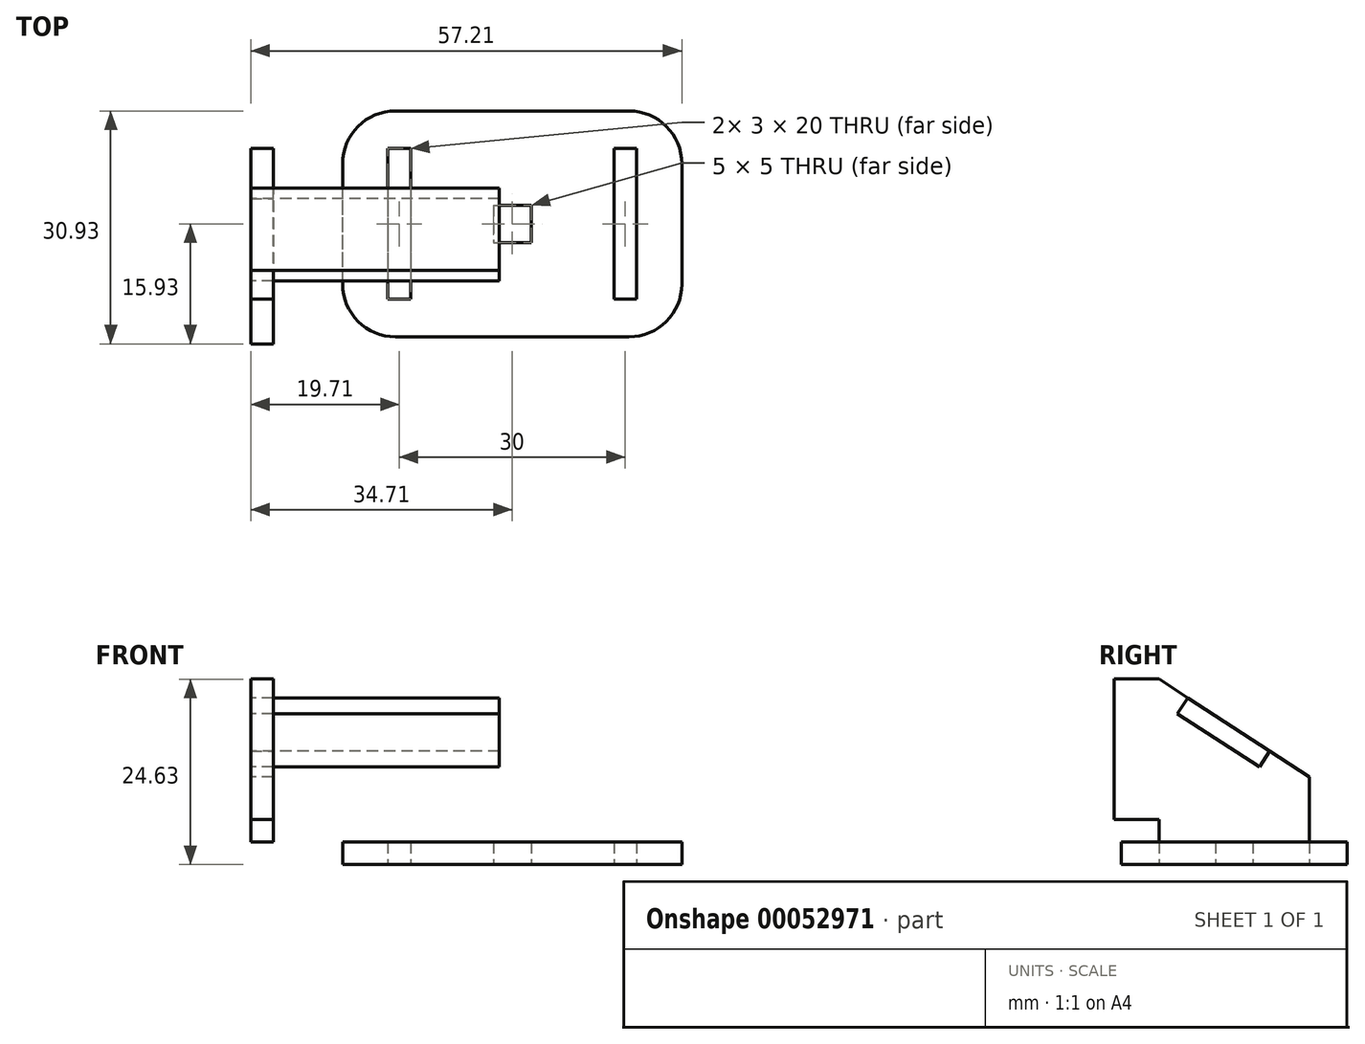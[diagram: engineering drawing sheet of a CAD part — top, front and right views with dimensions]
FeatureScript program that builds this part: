
annotation { "Feature Type Name" : "Feature", "Feature Type Description" : "" }
export const myFeature = defineFeature(function(context is Context, id is Id, definition is map)
    precondition{}
    {
        {
            var Q0;
            Q0=qCreatedBy(makeId("Top.planeOp"),FACE);
            var sketch = newSketch(context, id + "F0", { "sketchPlane" : qUnion([Q0])});
            skLineSegment(sketch, "E0.rect.bottom", {"start": v(-2.5, 2.5) * mm, "end": v(2.5, 2.5) * mm});
            skLineSegment(sketch, "E0.rect.top", {"start": v(-2.5, -2.5) * mm, "end": v(2.5, -2.5) * mm});
            skLineSegment(sketch, "E0.rect.left", {"start": v(-2.5, 2.5) * mm, "end": v(-2.5, -2.5) * mm});
            skLineSegment(sketch, "E0.rect.right", {"start": v(2.5, 2.5) * mm, "end": v(2.5, -2.5) * mm});
            skPoint(sketch, "E0.rect.middle", {"position": v(0, 0) * mm});
            skLineSegment(sketch, "E1.rect.bottom", {"start": v(-22.5, -15) * mm, "end": v(22.5, -15) * mm});
            skLineSegment(sketch, "E1.rect.top", {"start": v(-22.5, 15) * mm, "end": v(22.5, 15) * mm});
            skLineSegment(sketch, "E1.rect.left", {"start": v(-22.5, -15) * mm, "end": v(-22.5, 15) * mm});
            skLineSegment(sketch, "E1.rect.right", {"start": v(22.5, -15) * mm, "end": v(22.5, 15) * mm});
            skLineSegment(sketch, "E2.bottom", {"start": v(13.5, 10) * mm, "end": v(16.5, 10) * mm});
            skLineSegment(sketch, "E2.top", {"start": v(13.5, -10) * mm, "end": v(16.5, -10) * mm});
            skLineSegment(sketch, "E2.left", {"start": v(13.5, 10) * mm, "end": v(13.5, -10) * mm});
            skLineSegment(sketch, "E2.right", {"start": v(16.5, 10) * mm, "end": v(16.5, -10) * mm});
            skLineSegment(sketch, "E3.bottom", {"start": v(-16.5, 10) * mm, "end": v(-13.5, 10) * mm});
            skLineSegment(sketch, "E3.top", {"start": v(-16.5, -10) * mm, "end": v(-13.5, -10) * mm});
            skLineSegment(sketch, "E3.left", {"start": v(-16.5, 10) * mm, "end": v(-16.5, -10) * mm});
            skLineSegment(sketch, "E3.right", {"start": v(-13.5, 10) * mm, "end": v(-13.5, -10) * mm});
            skLineSegment(sketch, "E4", {"start": v(16.5, 10) * mm, "end": v(16.5, 15) * mm, "construction": true});
            skLineSegment(sketch, "E5", {"start": v(16.5, -10) * mm, "end": v(16.5, -15) * mm, "construction": true});
            skLineSegment(sketch, "E6", {"start": v(-16.5, 10) * mm, "end": v(-22.5, 10) * mm, "construction": true});
            skLineSegment(sketch, "E7", {"start": v(16.5, 10) * mm, "end": v(22.5, 10) * mm, "construction": true});
            skSolve(sketch);
        }
        {
            var Q0;
            Q0 = qSketchRegion(id + "F0", true);
            extrude(context, id + "F1", {"entities" : qUnion([Q0]), "depth" : 3 * mm});
        }
        {
            var Q0;
            Q0=makeQuery(id+"F1.opExtrude","SWEPT_EDGE",EDGE,{"disambiguationData":[OSD([sQuery(id+"F0.wireOp",EDGE,"E1.rect.top"),sQuery(id+"F0.wireOp",EDGE,"E1.rect.left")])]});
            var Q1;
            Q1=makeQuery(id+"F1.opExtrude","SWEPT_EDGE",EDGE,{"disambiguationData":[OSD([sQuery(id+"F0.wireOp",EDGE,"E1.rect.bottom"),sQuery(id+"F0.wireOp",EDGE,"E1.rect.left")])]});
            var Q2;
            Q2=makeQuery(id+"F1.opExtrude","SWEPT_EDGE",EDGE,{"disambiguationData":[OSD([sQuery(id+"F0.wireOp",EDGE,"E1.rect.bottom"),sQuery(id+"F0.wireOp",EDGE,"E1.rect.right")])]});
            var Q3;
            Q3=makeQuery(id+"F1.opExtrude","SWEPT_EDGE",EDGE,{"disambiguationData":[OSD([sQuery(id+"F0.wireOp",EDGE,"E1.rect.top"),sQuery(id+"F0.wireOp",EDGE,"E1.rect.right")])]});
            fillet(context, id + "F2", {"entities" : qUnion([Q0, Q1, Q2, Q3]), "radius" : 7 * mm, "tangentPropagation" : true, "allowEdgeOverflow" : false});
        }
        {
            var Q0;
            Q0=makeQuery(id+"F1.opExtrude","CAP_FACE",FACE,{"disambiguationData":[OSD([sQuery(id+"F0.wireOp",EDGE,"E0.rect.bottom"),sQuery(id+"F0.wireOp",EDGE,"E0.rect.top"),sQuery(id+"F0.wireOp",EDGE,"E0.rect.left"),sQuery(id+"F0.wireOp",EDGE,"E0.rect.right"),sQuery(id+"F0.wireOp",EDGE,"E1.rect.bottom"),sQuery(id+"F0.wireOp",EDGE,"E1.rect.top"),sQuery(id+"F0.wireOp",EDGE,"E1.rect.left"),sQuery(id+"F0.wireOp",EDGE,"E1.rect.right"),sQuery(id+"F0.wireOp",EDGE,"E2.bottom"),sQuery(id+"F0.wireOp",EDGE,"E2.top"),sQuery(id+"F0.wireOp",EDGE,"E2.left"),sQuery(id+"F0.wireOp",EDGE,"E2.right"),sQuery(id+"F0.wireOp",EDGE,"E3.bottom"),sQuery(id+"F0.wireOp",EDGE,"E3.top"),sQuery(id+"F0.wireOp",EDGE,"E3.left"),sQuery(id+"F0.wireOp",EDGE,"E3.right")])],"isStart":false});
            var sketch = newSketch(context, id + "F3", { "sketchPlane" : qUnion([Q0])});
            skLineSegment(sketch, "E8", {"start": v(-16.5, 10) * mm, "end": v(-41.32, 10) * mm, "construction": true});
            skLineSegment(sketch, "E9", {"start": v(-16.5, -10) * mm, "end": v(-42.8, -10) * mm, "construction": true});
            skLineSegment(sketch, "E10.bottom", {"start": v(-31.71, 10) * mm, "end": v(-34.71, 10) * mm});
            skLineSegment(sketch, "E10.top", {"start": v(-31.71, -10) * mm, "end": v(-34.71, -10) * mm});
            skLineSegment(sketch, "E10.left", {"start": v(-31.71, 10) * mm, "end": v(-31.71, -10) * mm});
            skLineSegment(sketch, "E10.right", {"start": v(-34.71, 10) * mm, "end": v(-34.71, -10) * mm});
            skSolve(sketch);
        }
        {
            var Q0;
            Q0=makeQuery(id+"F3.imprint","IMPRINT",FACE,{"disambiguationData":[TD([[makeQuery(id+"F3.imprint","IMPRINT",EDGE,{"derivedFrom":sQuery(id+"F3.wireOp",EDGE,"E10.bottom")}),1.0]])]});
            extrude(context, id + "F4", {"entities" : qUnion([Q0]), "depth" : 3 * mm});
        }
        {
            var Q0;
            Q0=makeQuery(id+"F4.opExtrude","SWEPT_FACE",FACE,{"disambiguationData":[OSD([sQuery(id+"F3.wireOp",EDGE,"E10.right")])]});
            var sketch = newSketch(context, id + "F5", { "sketchPlane" : qUnion([Q0])});
            skLineSegment(sketch, "E11", {"start": v(10, 24.63) * mm, "end": v(10, 6) * mm});
            skLineSegment(sketch, "E12", {"start": v(10, 6) * mm, "end": v(-10, 6) * mm});
            skLineSegment(sketch, "E13.bottom", {"start": v(10, 6) * mm, "end": v(15.93, 6) * mm});
            skLineSegment(sketch, "E13.top", {"start": v(10, 24.63) * mm, "end": v(15.93, 24.63) * mm});
            skLineSegment(sketch, "E13.left", {"start": v(10, 6) * mm, "end": v(10, 24.63) * mm});
            skLineSegment(sketch, "E13.right", {"start": v(15.93, 6) * mm, "end": v(15.93, 24.63) * mm});
            skLineSegment(sketch, "E14", {"start": v(-10, 6) * mm, "end": v(-10, 11.63) * mm});
            skLineSegment(sketch, "E15", {"start": v(-10, 11.63) * mm, "end": v(10, 24.63) * mm});
            skSolve(sketch);
        }
        {
            var Q0;
            Q0=makeQuery(id+"F5.imprint","IMPRINT",FACE,{"disambiguationData":[TD([[makeQuery(id+"F5.imprint","IMPRINT",EDGE,{"derivedFrom":sQuery(id+"F5.wireOp",EDGE,"E13.bottom")}),1.0]])]});
            var Q1;
            Q1=makeQuery(id+"F5.imprint","IMPRINT",FACE,{"disambiguationData":[TD([[makeQuery(id+"F5.imprint","IMPRINT",EDGE,{"derivedFrom":sQuery(id+"F5.wireOp",EDGE,"E12")}),1.0]])]});
            extrude(context, id + "F6", {"entities" : qUnion([Q0, Q1]), "operationType" : NewBodyOperationType.ADD, "oppositeDirection" : true, "depth" : 3 * mm});
        }
        {
            var Q0;
            Q0=makeQuery(id+"F6.boolean.opBoolean","MERGE",FACE,{"derivedFrom":[makeQuery(id+"F4.opExtrude","SWEPT_FACE",FACE,{"disambiguationData":[OSD([sQuery(id+"F3.wireOp",EDGE,"E10.left")])]}),makeQuery(id+"F6.opExtrude","CAP_FACE",FACE,{"disambiguationData":[OSD([sQuery(id+"F5.wireOp",EDGE,"E12"),sQuery(id+"F5.wireOp",EDGE,"E13.bottom"),sQuery(id+"F5.wireOp",EDGE,"E13.top"),sQuery(id+"F5.wireOp",EDGE,"E13.right"),sQuery(id+"F5.wireOp",EDGE,"E14"),sQuery(id+"F5.wireOp",EDGE,"E15")])],"isStart":false})]});
            var sketch = newSketch(context, id + "F7", { "sketchPlane" : qUnion([Q0])});
            skLineSegment(sketch, "E16", {"start": v(-6.17, 22.15) * mm, "end": v(-7.54, 20.05) * mm});
            skLineSegment(sketch, "E17", {"start": v(-7.54, 20.05) * mm, "end": v(3.36, 12.96) * mm});
            skLineSegment(sketch, "E18", {"start": v(3.36, 12.96) * mm, "end": v(4.72, 15.06) * mm});
            skLineSegment(sketch, "E19", {"start": v(4.72, 15.06) * mm, "end": v(-6.17, 22.15) * mm});
            skSolve(sketch);
        }
        {
            var Q0;
            Q0=makeQuery(id+"F7.imprint","IMPRINT",FACE,{"disambiguationData":[TD([[makeQuery(id+"F7.imprint","IMPRINT",EDGE,{"derivedFrom":sQuery(id+"F7.wireOp",EDGE,"E16")}),1.0]])]});
            extrude(context, id + "F8", {"entities" : qUnion([Q0]), "operationType" : NewBodyOperationType.REMOVE, "oppositeDirection" : true, "depth" : 25 * mm});
        }
        {
            var Q0;
            Q0=makeQuery(id+"F6.boolean.opBoolean","MERGE",FACE,{"derivedFrom":[makeQuery(id+"F4.opExtrude","SWEPT_FACE",FACE,{"disambiguationData":[OSD([sQuery(id+"F3.wireOp",EDGE,"E10.right")])]}),makeQuery(id+"F6.opExtrude","CAP_FACE",FACE,{"disambiguationData":[OSD([sQuery(id+"F5.wireOp",EDGE,"E12"),sQuery(id+"F5.wireOp",EDGE,"E13.bottom"),sQuery(id+"F5.wireOp",EDGE,"E13.top"),sQuery(id+"F5.wireOp",EDGE,"E13.right"),sQuery(id+"F5.wireOp",EDGE,"E14"),sQuery(id+"F5.wireOp",EDGE,"E15")])],"isStart":true})]});
            var sketch = newSketch(context, id + "F9", { "sketchPlane" : qUnion([Q0])});
            skLineSegment(sketch, "E20.0", {"start": v(7.54, 20.05) * mm, "end": v(-3.36, 12.96) * mm});
            skLineSegment(sketch, "E21.0", {"start": v(6.17, 22.15) * mm, "end": v(7.54, 20.05) * mm});
            skLineSegment(sketch, "E22.0", {"start": v(-3.36, 12.96) * mm, "end": v(-4.72, 15.06) * mm});
            skLineSegment(sketch, "E23", {"start": v(-4.72, 15.06) * mm, "end": v(6.17, 22.15) * mm});
            skSolve(sketch);
        }
        {
            var Q0;
            Q0=makeQuery(id+"F9.imprint","IMPRINT",FACE,{"disambiguationData":[TD([[makeQuery(id+"F9.imprint","IMPRINT",EDGE,{"derivedFrom":sQuery(id+"F9.wireOp",EDGE,"E20.0")}),-1.0]])]});
            extrude(context, id + "F10", {"entities" : qUnion([Q0]), "oppositeDirection" : true, "depth" : 33 * mm});
        }
    });
